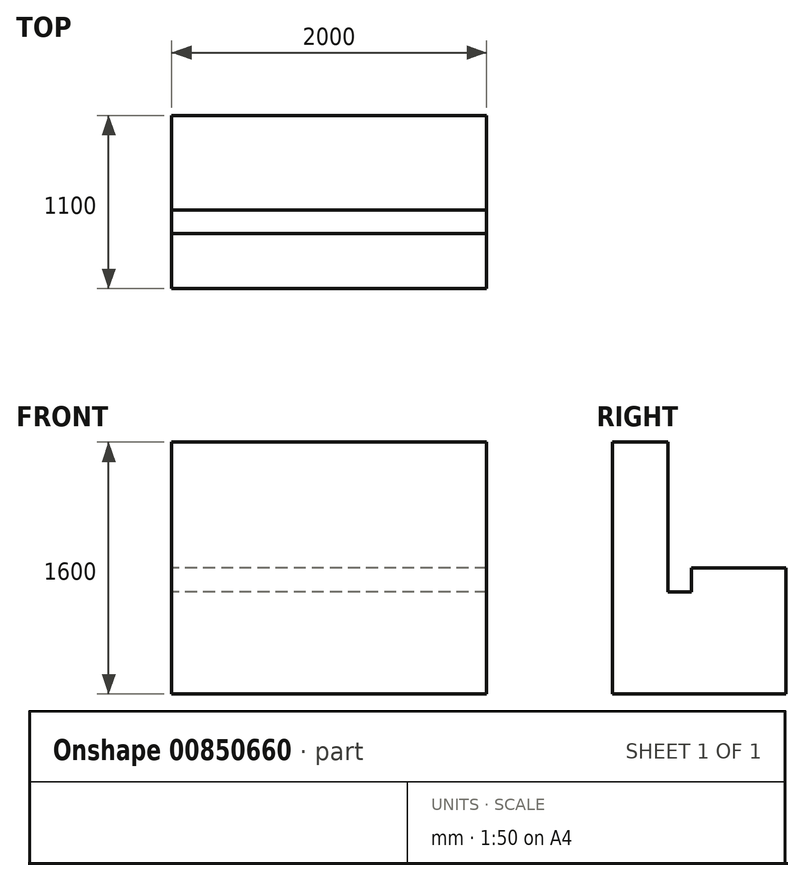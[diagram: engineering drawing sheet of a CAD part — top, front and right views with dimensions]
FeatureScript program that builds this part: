
annotation { "Feature Type Name" : "Feature", "Feature Type Description" : "" }
export const myFeature = defineFeature(function(context is Context, id is Id, definition is map)
    precondition{}
    {
        {
            var Q0;
            Q0=qCreatedBy(makeId("Right.planeOp"),FACE);
            var sketch = newSketch(context, id + "F0", { "sketchPlane" : qUnion([Q0])});
            skLineSegment(sketch, "E0", {"start": v(-51.62, 1549.28) * mm, "end": v(-51.62, -50.72) * mm});
            skLineSegment(sketch, "E1", {"start": v(-51.62, -50.72) * mm, "end": v(1048.38, -50.72) * mm});
            skLineSegment(sketch, "E2", {"start": v(1048.38, -50.72) * mm, "end": v(1048.38, 749.28) * mm});
            skLineSegment(sketch, "E3", {"start": v(298.38, 749.28) * mm, "end": v(298.38, 1549.28) * mm});
            skLineSegment(sketch, "E4", {"start": v(298.38, 1549.28) * mm, "end": v(-51.62, 1549.28) * mm});
            skLineSegment(sketch, "E5", {"start": v(1048.38, 749.28) * mm, "end": v(448.38, 749.28) * mm});
            skLineSegment(sketch, "E6", {"start": v(448.38, 749.28) * mm, "end": v(448.38, 599.28) * mm});
            skLineSegment(sketch, "E7", {"start": v(448.38, 599.28) * mm, "end": v(298.38, 599.28) * mm});
            skLineSegment(sketch, "E8", {"start": v(298.38, 599.28) * mm, "end": v(298.38, 749.28) * mm});
            skSolve(sketch);
        }
        {
            var Q0;
            Q0 = qSketchRegion(id + "F0", true);
            extrude(context, id + "F1", {"entities" : qUnion([Q0]), "depth" : 2000 * mm, "offsetDistance" : 25 * mm});
        }
    });
